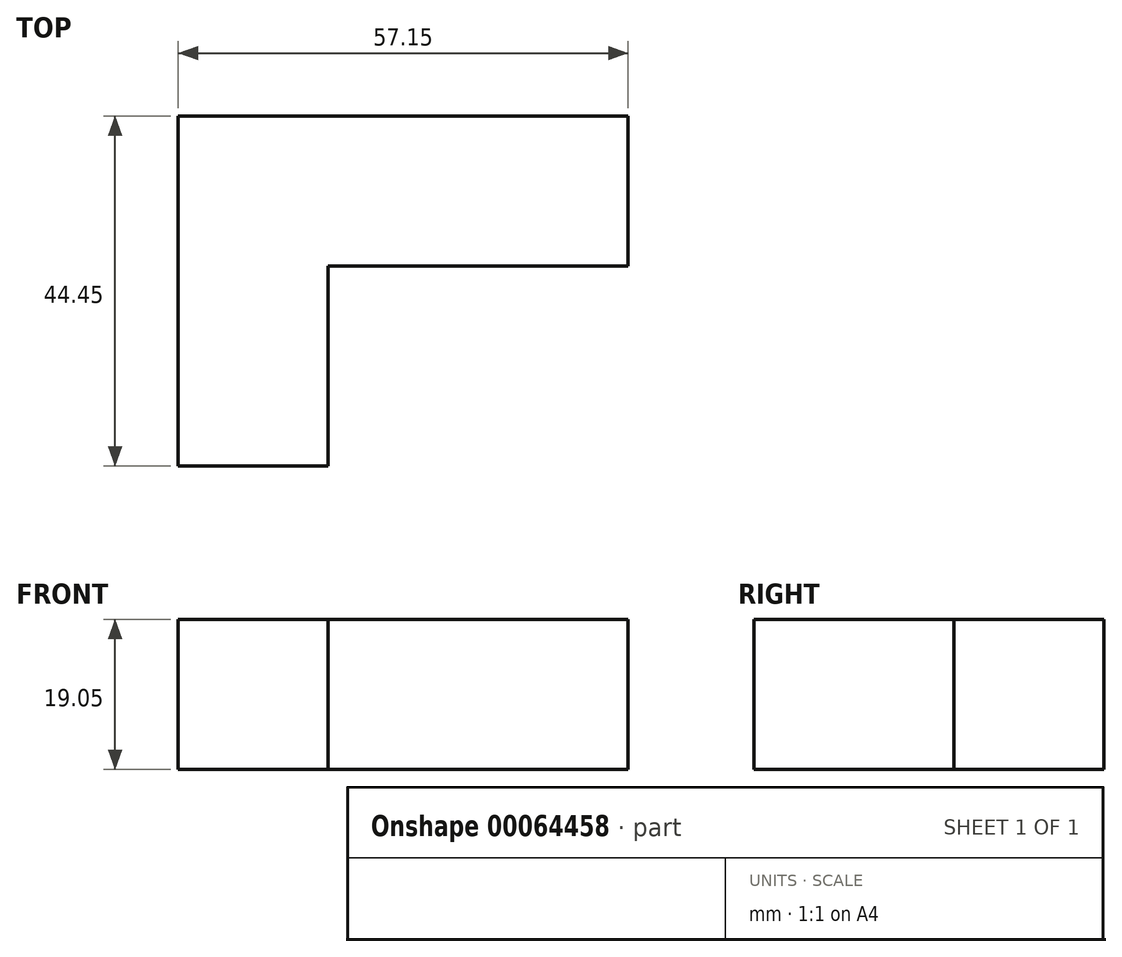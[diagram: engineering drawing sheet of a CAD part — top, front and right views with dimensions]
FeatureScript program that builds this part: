
annotation { "Feature Type Name" : "Feature", "Feature Type Description" : "" }
export const myFeature = defineFeature(function(context is Context, id is Id, definition is map)
    precondition{}
    {
        {
            var Q0;
            Q0=qCreatedBy(makeId("Front.planeOp"),FACE);
            var sketch = newSketch(context, id + "F0", { "sketchPlane" : qUnion([Q0])});
            skLineSegment(sketch, "E0.bottom", {"start": v(0, 0) * mm, "end": v(57.15, 0) * mm});
            skLineSegment(sketch, "E0.top", {"start": v(0, 19.05) * mm, "end": v(57.15, 19.05) * mm});
            skLineSegment(sketch, "E0.left", {"start": v(0, 0) * mm, "end": v(0, 19.05) * mm});
            skLineSegment(sketch, "E0.right", {"start": v(57.15, 0) * mm, "end": v(57.15, 19.05) * mm});
            skLineSegment(sketch, "E1.bottom", {"start": v(0, 19.05) * mm, "end": v(19.05, 19.05) * mm});
            skLineSegment(sketch, "E1.top", {"start": v(0, 57.15) * mm, "end": v(19.05, 57.15) * mm});
            skLineSegment(sketch, "E1.left", {"start": v(0, 19.05) * mm, "end": v(0, 57.15) * mm});
            skLineSegment(sketch, "E1.right", {"start": v(19.05, 19.05) * mm, "end": v(19.05, 57.15) * mm});
            skSolve(sketch);
        }
        {
            var Q0;
            Q0=makeQuery(id+"F0.imprint","IMPRINT",FACE,{"disambiguationData":[TD([[makeQuery(id+"F0.imprint","IMPRINT",EDGE,{"derivedFrom":sQuery(id+"F0.wireOp",EDGE,"E0.bottom")}),1.0]])]});
            var Q1;
            Q1=makeQuery(id+"F0.imprint","IMPRINT",FACE,{"disambiguationData":[TD([[makeQuery(id+"F0.imprint","IMPRINT",EDGE,{"derivedFrom":sQuery(id+"F0.wireOp",EDGE,"E1.bottom")}),1.0]])]});
            extrude(context, id + "F1", {"entities" : qUnion([Q0, Q1]), "flatOperationType" : FlatOperationType.REMOVE, "thickness" : 6.35 * mm, "thickness2" : 0 * mm, "thickness1" : 6.35 * mm, "startOffsetDistance" : 25.4 * mm, "startOffsetBound" : StartOffsetType.BLIND, "offsetDistance" : 25.4 * mm, "depth" : 19.05 * mm, "domain" : OperationDomain.MODEL});
        }
        {
            var Q0;
            Q0=makeQuery(id+"F1.opExtrude","CAP_FACE",FACE,{"disambiguationData":[OSD([sQuery(id+"F0.wireOp",EDGE,"E0.bottom"),sQuery(id+"F0.wireOp",EDGE,"E0.top"),sQuery(id+"F0.wireOp",EDGE,"E0.left"),sQuery(id+"F0.wireOp",EDGE,"E0.right")])],"isStart":false});
            var sketch = newSketch(context, id + "F2", { "sketchPlane" : qUnion([Q0])});
            skLineSegment(sketch, "E2.bottom", {"start": v(0, 0) * mm, "end": v(19.05, 0) * mm});
            skLineSegment(sketch, "E2.top", {"start": v(0, 19.05) * mm, "end": v(19.05, 19.05) * mm});
            skLineSegment(sketch, "E2.left", {"start": v(0, 0) * mm, "end": v(0, 19.05) * mm});
            skLineSegment(sketch, "E2.right", {"start": v(19.05, 0) * mm, "end": v(19.05, 19.05) * mm});
            skSolve(sketch);
        }
        {
            var Q0;
            Q0=makeQuery(id+"F2.imprint","IMPRINT",FACE,{"disambiguationData":[TD([[makeQuery(id+"F2.imprint","IMPRINT",EDGE,{"derivedFrom":sQuery(id+"F2.wireOp",EDGE,"E2.bottom")}),1.0]])]});
            extrude(context, id + "F3", {"entities" : qUnion([Q0]), "operationType" : NewBodyOperationType.ADD, "depth" : 25.4 * mm});
        }
    });
